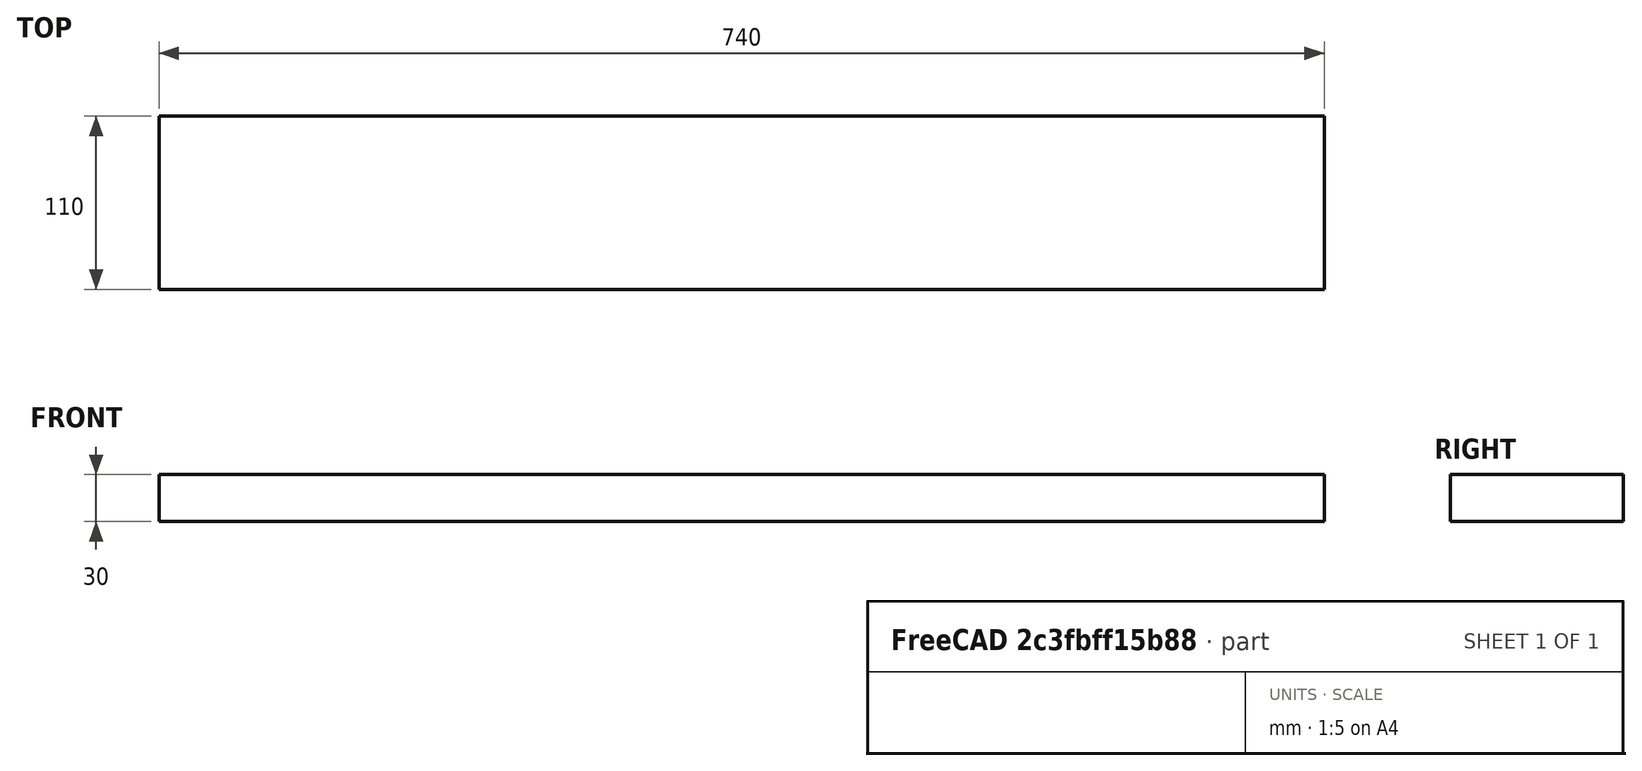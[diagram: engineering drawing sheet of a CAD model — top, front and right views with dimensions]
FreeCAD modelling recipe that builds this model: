
FCSTD DOCUMENT  (FreeCAD 1.0R39109 (Git))
Label: 025_table_frame_side_right
License: All rights reserved
LicenseURL: http://en.wikipedia.org/wiki/All_rights_reserved
objects: Spreadsheet::Sheet×1, Sketcher::SketchObject×1, PartDesign::Pad×1, PartDesign::Body×1
note: 6 computed .brp shape members not serialized (recipe doc carries the construction recipe); baked Part::Feature solids carry a one-line shape summary decoded from their .brp

FEATURE [Spreadsheet::Sheet] Spreadsheet
  cells = A4='length; B4(length)=800; A5='width; B5(width)=110; A6='height; B6(height)=30
FEATURE [Sketcher::SketchObject] Sketch
  ArcFitTolerance = 1e-06
  AttachmentSupport = -> [XY_Plane]
  FullyConstrained = true
  MakeInternals = false
  MapMode = 5
  expr: Constraints[11] = Spreadsheet.length - 2 * Spreadsheet.height
  expr: Constraints[12] = Spreadsheet.width
  sketch-geometry (5):
    g0: LineSegment StartX=-370 StartY=55 StartZ=0 EndX=-370 EndY=-55 EndZ=0
    g1: LineSegment StartX=-370 StartY=-55 StartZ=0 EndX=370 EndY=-55 EndZ=0
    g2: LineSegment StartX=370 StartY=-55 StartZ=0 EndX=370 EndY=55 EndZ=0
    g3: LineSegment StartX=370 StartY=55 StartZ=0 EndX=-370 EndY=55 EndZ=0
    g4: LineSegment [constr] StartX=-370 StartY=55 StartZ=0 EndX=370 EndY=-55 EndZ=0
  constraints (13):
    c: Coincident(g0,g1)
    c: Coincident(g1,g2)
    c: Coincident(g2,g3)
    c: Coincident(g3,g0)
    c: Vertical(g0)
    c: Vertical(g2)
    c: Horizontal(g1)
    c: Horizontal(g3)
    c: Coincident(g4,g0)
    c: Coincident(g4,g1)
    c: Symmetric(g4,g4,g-1)
    c: DistanceX(g3,g3) = 740
    c: DistanceY(g0,g0) = 110
FEATURE [PartDesign::Pad] Pad
  Direction = (0,0,1)
  Length = 30
  Length2 = 10
  Midplane = true
  Profile = -> Sketch
  ReferenceAxis = -> Sketch [N_Axis]
  Suppressed = false
  Type = 0
  expr: Length = Spreadsheet.height
FEATURE [PartDesign::Body] Body
  AllowCompound = false
  Group = -> [Sketch,Pad]
  Origin = -> Origin
  Tip = -> Pad
